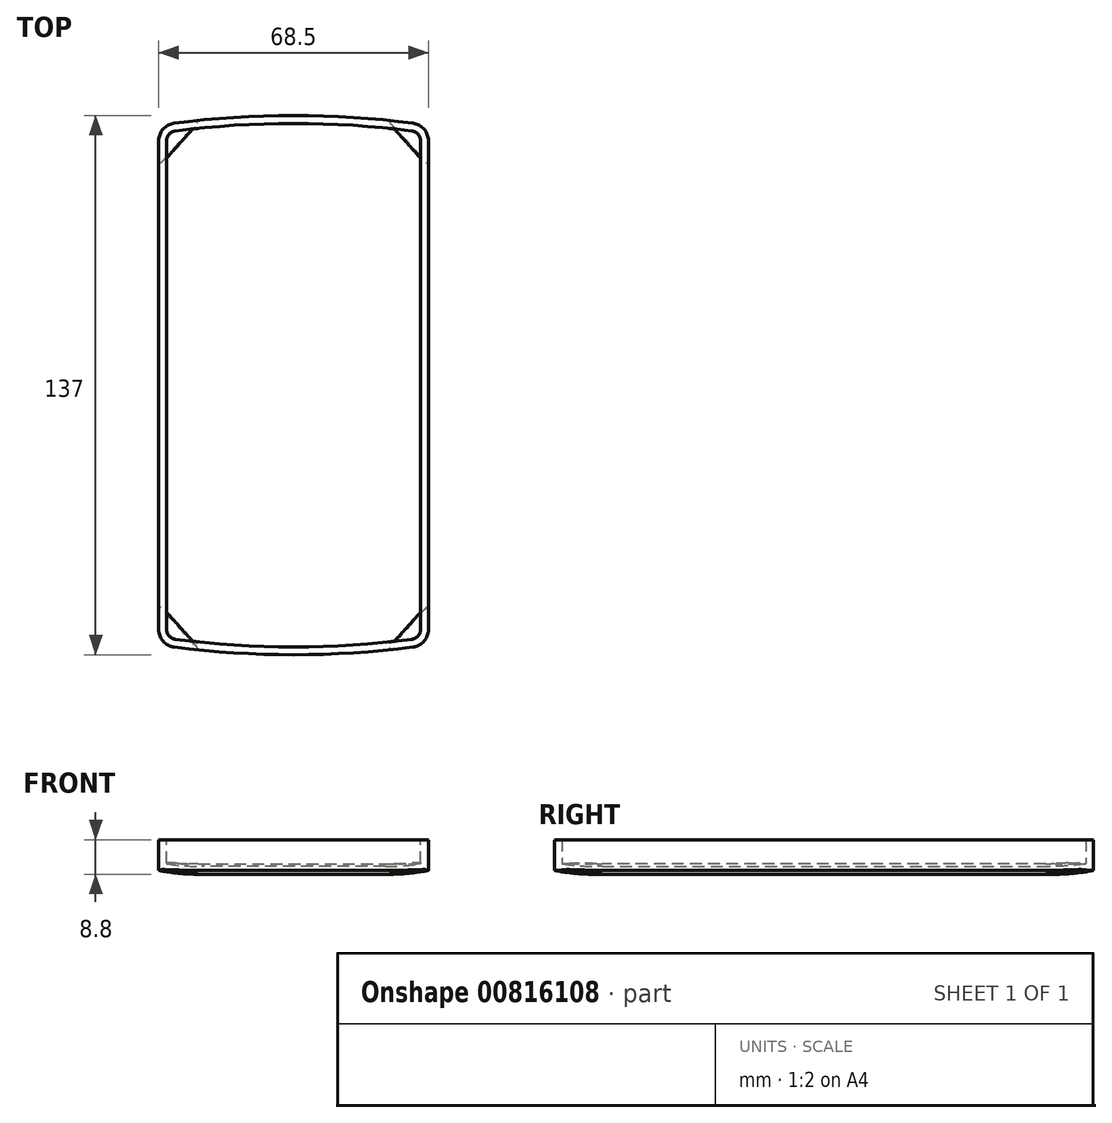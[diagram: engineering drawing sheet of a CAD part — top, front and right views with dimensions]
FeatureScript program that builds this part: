
annotation { "Feature Type Name" : "Feature", "Feature Type Description" : "" }
export const myFeature = defineFeature(function(context is Context, id is Id, definition is map)
    precondition{}
    {
        {
            var Q0;
            Q0=qCreatedBy(makeId("Top.planeOp"),FACE);
            var sketch = newSketch(context, id + "F0", { "sketchPlane" : qUnion([Q0])});
            skLineSegment(sketch, "E0.bottom", {"start": v(34.25, -68.5) * mm, "end": v(-34.25, -68.5) * mm, "construction": true});
            skLineSegment(sketch, "E0.top", {"start": v(34.25, 68.5) * mm, "end": v(-34.25, 68.5) * mm, "construction": true});
            skLineSegment(sketch, "E0.left", {"start": v(34.25, -68.5) * mm, "end": v(34.25, -66) * mm, "construction": true});
            skLineSegment(sketch, "E0.right", {"start": v(-34.25, -68.5) * mm, "end": v(-34.25, -66) * mm, "construction": true});
            skPoint(sketch, "E0.middle", {"position": v(0, 0) * mm});
            skPoint(sketch, "E1", {"position": v(0, -68.5) * mm});
            skPoint(sketch, "E2", {"position": v(0, 68.5) * mm});
            skLineSegment(sketch, "E3", {"start": v(34.25, 66) * mm, "end": v(34.25, 68.5) * mm, "construction": true});
            skLineSegment(sketch, "E4", {"start": v(34.25, -66) * mm, "end": v(34.25, 66) * mm});
            skLineSegment(sketch, "E5", {"start": v(-34.25, -66) * mm, "end": v(-34.25, 66) * mm});
            skLineSegment(sketch, "E6", {"start": v(-34.25, 66) * mm, "end": v(-34.25, 68.5) * mm, "construction": true});
            skArc(sketch, "E7", {"start": v(-34.25, -66) * mm, "mid": v(0, -68.5) * mm, "end": v(34.25, -66) * mm});
            skArc(sketch, "E8", {"start": v(34.25, 66) * mm, "mid": v(0, 68.5) * mm, "end": v(-34.25, 66) * mm});
            skSolve(sketch);
        }
        {
            var Q0;
            Q0=makeQuery(id+"F0.imprint","IMPRINT",FACE,{"disambiguationData":[TD([[makeQuery(id+"F0.imprint","IMPRINT",EDGE,{"derivedFrom":sQuery(id+"F0.wireOp",EDGE,"E0.bottom")}),-1.0]])]});
            var Q1;
            Q1=makeQuery(id+"F0.imprint","IMPRINT",FACE,{"disambiguationData":[TD([[makeQuery(id+"F0.imprint","IMPRINT",EDGE,{"derivedFrom":sQuery(id+"F0.wireOp",EDGE,"E4")}),1.0]])]});
            extrude(context, id + "F1", {"entities" : qUnion([Q0, Q1]), "depth" : 7.8 * mm, "offsetDistance" : 25 * mm});
        }
        {
            var Q0;
            Q0=makeQuery(id+"F1.opExtrude","SWEPT_EDGE",EDGE,{"disambiguationData":[OSD([sQuery(id+"F0.wireOp",EDGE,"E5"),sQuery(id+"F0.wireOp",EDGE,"E7")])]});
            var Q1;
            Q1=makeQuery(id+"F1.opExtrude","SWEPT_EDGE",EDGE,{"disambiguationData":[OSD([sQuery(id+"F0.wireOp",EDGE,"E4"),sQuery(id+"F0.wireOp",EDGE,"E7")])]});
            var Q2;
            Q2=makeQuery(id+"F1.opExtrude","SWEPT_EDGE",EDGE,{"disambiguationData":[OSD([sQuery(id+"F0.wireOp",EDGE,"E5"),sQuery(id+"F0.wireOp",EDGE,"E8")])]});
            var Q3;
            Q3=makeQuery(id+"F1.opExtrude","SWEPT_EDGE",EDGE,{"disambiguationData":[OSD([sQuery(id+"F0.wireOp",EDGE,"E4"),sQuery(id+"F0.wireOp",EDGE,"E8")])]});
            fillet(context, id + "F2", {"entities" : qUnion([Q0, Q1, Q2, Q3]), "radius" : 4.5 * mm, "tangentPropagation" : true, "allowEdgeOverflow" : false});
        }
        {
            var Q0;
            Q0=makeQuery(id+"F1.opExtrude","CAP_FACE",FACE,{"disambiguationData":[OSD([sQuery(id+"F0.wireOp",EDGE,"E4"),sQuery(id+"F0.wireOp",EDGE,"E5"),sQuery(id+"F0.wireOp",EDGE,"E7"),sQuery(id+"F0.wireOp",EDGE,"E8")])],"isStart":true});
            extrude(context, id + "F3", {"entities" : qUnion([Q0]), "operationType" : NewBodyOperationType.ADD, "depth" : 1 * mm, "offsetDistance" : 25 * mm, "hasDraft" : true, "draftAngle" : 80 * degree, "draftPullDirection" : true});
        }
        {
            var Q0;
            Q0=makeQuery(id+"F3.opExtrude","CAP_EDGE",EDGE,{"disambiguationData":[OSD([sQuery(id+"F0.wireOp",EDGE,"E7")])],"isStart":false});
            var Q1;
            Q1=makeQuery(id+"F3.opExtrude","CAP_EDGE",EDGE,{"disambiguationData":[OSD([sQuery(id+"F0.wireOp",EDGE,"E5")])],"isStart":false});
            var Q2;
            Q2=makeQuery(id+"F3.opExtrude","CAP_EDGE",EDGE,{"disambiguationData":[OSD([sQuery(id+"F0.wireOp",EDGE,"E8")])],"isStart":false});
            var Q3;
            Q3=makeQuery(id+"F3.opExtrude","CAP_EDGE",EDGE,{"disambiguationData":[OSD([sQuery(id+"F0.wireOp",EDGE,"E4")])],"isStart":false});
            var Q4;
            {var subQ0=sQuery(id+"F0.wireOp",EDGE,"E8");var subQ1=sQuery(id+"F0.wireOp",EDGE,"E7");var subQ2=sQuery(id+"F0.wireOp",EDGE,"E5");var subQ3=sQuery(id+"F0.wireOp",EDGE,"E4");var subQ4=makeQuery(id+"F1.opExtrude","CAP_FACE",FACE,{"disambiguationData":[OSD([subQ3,subQ2,subQ1,subQ0])],"isStart":true});var subQ5=makeQuery(id+"F1.opExtrude","SWEPT_EDGE",EDGE,{"disambiguationData":[OSD([subQ3,subQ0])]});Q4=makeQuery(id+"F3.*.draft.opDraft","MERGE",EDGE,{"derivedFrom":[makeQuery(id+"F3.opExtrude","SWEPT_EDGE",EDGE,{"disambiguationData":[OSD([subQ3,subQ2,subQ1,subQ0]),TDD([makeQuery(id+"F2.opFillet","BLEND_VERTEX",VERTEX,{"blendedFrom":[subQ5,makeQuery(id+"F1.opExtrude","SWEPT_FACE",FACE,{"disambiguationData":[OSD([subQ3])]}),subQ4],"blendedInto":[makeQuery(id+"F1.opExtrude","SWEPT_FACE",FACE,{"disambiguationData":[OSD([subQ3])]}),subQ4]})])]}),makeQuery(id+"F3.opExtrude","SWEPT_EDGE",EDGE,{"disambiguationData":[OSD([subQ3,subQ2,subQ1,subQ0]),TDD([makeQuery(id+"F2.opFillet","BLEND_VERTEX",VERTEX,{"blendedFrom":[subQ5,subQ4,makeQuery(id+"F1.opExtrude","SWEPT_FACE",FACE,{"disambiguationData":[OSD([subQ0])]})],"blendedInto":[subQ4,makeQuery(id+"F1.opExtrude","SWEPT_FACE",FACE,{"disambiguationData":[OSD([subQ0])]})]})])]})]});}
            var Q5;
            {var subQ0=sQuery(id+"F0.wireOp",EDGE,"E8");var subQ1=sQuery(id+"F0.wireOp",EDGE,"E7");var subQ2=sQuery(id+"F0.wireOp",EDGE,"E5");var subQ3=sQuery(id+"F0.wireOp",EDGE,"E4");Q5=makeQuery(id+"F3.*.draft.opDraft","SPLIT",EDGE,{"derivedFrom":makeQuery(id+"F3.opExtrude","SWEPT_EDGE",EDGE,{"disambiguationData":[OSD([subQ3,subQ2,subQ1,subQ0]),TDD([makeQuery(id+"F2.opFillet","BLEND_VERTEX",VERTEX,{"blendedFrom":[makeQuery(id+"F1.opExtrude","SWEPT_EDGE",EDGE,{"disambiguationData":[OSD([subQ3,subQ0])]}),makeQuery(id+"F1.opExtrude","CAP_FACE",FACE,{"disambiguationData":[OSD([subQ3,subQ2,subQ1,subQ0])],"isStart":true}),makeQuery(id+"F1.opExtrude","SWEPT_FACE",FACE,{"disambiguationData":[OSD([subQ0])]})],"blendedInto":[makeQuery(id+"F1.opExtrude","CAP_FACE",FACE,{"disambiguationData":[OSD([subQ3,subQ2,subQ1,subQ0])],"isStart":true}),makeQuery(id+"F1.opExtrude","SWEPT_FACE",FACE,{"disambiguationData":[OSD([subQ0])]})]})])]})});}
            var Q6;
            {var subQ0=sQuery(id+"F0.wireOp",EDGE,"E8");var subQ1=sQuery(id+"F0.wireOp",EDGE,"E7");var subQ2=sQuery(id+"F0.wireOp",EDGE,"E5");var subQ3=sQuery(id+"F0.wireOp",EDGE,"E4");Q6=makeQuery(id+"F3.*.draft.opDraft","SPLIT",EDGE,{"derivedFrom":makeQuery(id+"F3.opExtrude","SWEPT_EDGE",EDGE,{"disambiguationData":[OSD([subQ3,subQ2,subQ1,subQ0]),TDD([makeQuery(id+"F2.opFillet","BLEND_VERTEX",VERTEX,{"blendedFrom":[makeQuery(id+"F1.opExtrude","SWEPT_EDGE",EDGE,{"disambiguationData":[OSD([subQ3,subQ0])]}),makeQuery(id+"F1.opExtrude","SWEPT_FACE",FACE,{"disambiguationData":[OSD([subQ3])]}),makeQuery(id+"F1.opExtrude","CAP_FACE",FACE,{"disambiguationData":[OSD([subQ3,subQ2,subQ1,subQ0])],"isStart":true})],"blendedInto":[makeQuery(id+"F1.opExtrude","SWEPT_FACE",FACE,{"disambiguationData":[OSD([subQ3])]}),makeQuery(id+"F1.opExtrude","CAP_FACE",FACE,{"disambiguationData":[OSD([subQ3,subQ2,subQ1,subQ0])],"isStart":true})]})])]})});}
            var Q7;
            {var subQ0=sQuery(id+"F0.wireOp",EDGE,"E8");var subQ1=sQuery(id+"F0.wireOp",EDGE,"E7");var subQ2=sQuery(id+"F0.wireOp",EDGE,"E5");var subQ3=sQuery(id+"F0.wireOp",EDGE,"E4");var subQ4=makeQuery(id+"F1.opExtrude","CAP_FACE",FACE,{"disambiguationData":[OSD([subQ3,subQ2,subQ1,subQ0])],"isStart":true});var subQ5=makeQuery(id+"F1.opExtrude","SWEPT_EDGE",EDGE,{"disambiguationData":[OSD([subQ2,subQ0])]});Q7=makeQuery(id+"F3.*.draft.opDraft","MERGE",EDGE,{"derivedFrom":[makeQuery(id+"F3.opExtrude","SWEPT_EDGE",EDGE,{"disambiguationData":[OSD([subQ3,subQ2,subQ1,subQ0]),TDD([makeQuery(id+"F2.opFillet","BLEND_VERTEX",VERTEX,{"blendedFrom":[subQ5,subQ4,makeQuery(id+"F1.opExtrude","SWEPT_FACE",FACE,{"disambiguationData":[OSD([subQ2])]})],"blendedInto":[subQ4,makeQuery(id+"F1.opExtrude","SWEPT_FACE",FACE,{"disambiguationData":[OSD([subQ2])]})]})])]}),makeQuery(id+"F3.opExtrude","SWEPT_EDGE",EDGE,{"disambiguationData":[OSD([subQ3,subQ2,subQ1,subQ0]),TDD([makeQuery(id+"F2.opFillet","BLEND_VERTEX",VERTEX,{"blendedFrom":[subQ5,subQ4,makeQuery(id+"F1.opExtrude","SWEPT_FACE",FACE,{"disambiguationData":[OSD([subQ0])]})],"blendedInto":[subQ4,makeQuery(id+"F1.opExtrude","SWEPT_FACE",FACE,{"disambiguationData":[OSD([subQ0])]})]})])]})]});}
            var Q8;
            {var subQ0=sQuery(id+"F0.wireOp",EDGE,"E8");var subQ1=sQuery(id+"F0.wireOp",EDGE,"E7");var subQ2=sQuery(id+"F0.wireOp",EDGE,"E5");var subQ3=sQuery(id+"F0.wireOp",EDGE,"E4");Q8=makeQuery(id+"F3.*.draft.opDraft","SPLIT",EDGE,{"derivedFrom":makeQuery(id+"F3.opExtrude","SWEPT_EDGE",EDGE,{"disambiguationData":[OSD([subQ3,subQ2,subQ1,subQ0]),TDD([makeQuery(id+"F2.opFillet","BLEND_VERTEX",VERTEX,{"blendedFrom":[makeQuery(id+"F1.opExtrude","SWEPT_EDGE",EDGE,{"disambiguationData":[OSD([subQ2,subQ0])]}),makeQuery(id+"F1.opExtrude","CAP_FACE",FACE,{"disambiguationData":[OSD([subQ3,subQ2,subQ1,subQ0])],"isStart":true}),makeQuery(id+"F1.opExtrude","SWEPT_FACE",FACE,{"disambiguationData":[OSD([subQ0])]})],"blendedInto":[makeQuery(id+"F1.opExtrude","CAP_FACE",FACE,{"disambiguationData":[OSD([subQ3,subQ2,subQ1,subQ0])],"isStart":true}),makeQuery(id+"F1.opExtrude","SWEPT_FACE",FACE,{"disambiguationData":[OSD([subQ0])]})]})])]})});}
            var Q9;
            {var subQ0=sQuery(id+"F0.wireOp",EDGE,"E5");var subQ1=sQuery(id+"F0.wireOp",EDGE,"E8");var subQ2=sQuery(id+"F0.wireOp",EDGE,"E7");var subQ3=sQuery(id+"F0.wireOp",EDGE,"E4");Q9=makeQuery(id+"F3.*.draft.opDraft","SPLIT",EDGE,{"derivedFrom":makeQuery(id+"F3.opExtrude","SWEPT_EDGE",EDGE,{"disambiguationData":[OSD([subQ3,subQ0,subQ2,subQ1]),TDD([makeQuery(id+"F2.opFillet","BLEND_VERTEX",VERTEX,{"blendedFrom":[makeQuery(id+"F1.opExtrude","SWEPT_EDGE",EDGE,{"disambiguationData":[OSD([subQ0,subQ1])]}),makeQuery(id+"F1.opExtrude","CAP_FACE",FACE,{"disambiguationData":[OSD([subQ3,subQ0,subQ2,subQ1])],"isStart":true}),makeQuery(id+"F1.opExtrude","SWEPT_FACE",FACE,{"disambiguationData":[OSD([subQ0])]})],"blendedInto":[makeQuery(id+"F1.opExtrude","CAP_FACE",FACE,{"disambiguationData":[OSD([subQ3,subQ0,subQ2,subQ1])],"isStart":true}),makeQuery(id+"F1.opExtrude","SWEPT_FACE",FACE,{"disambiguationData":[OSD([subQ0])]})]})])]})});}
            var Q10;
            {var subQ0=sQuery(id+"F0.wireOp",EDGE,"E5");var subQ1=sQuery(id+"F0.wireOp",EDGE,"E8");var subQ2=sQuery(id+"F0.wireOp",EDGE,"E7");var subQ3=sQuery(id+"F0.wireOp",EDGE,"E4");Q10=makeQuery(id+"F3.*.draft.opDraft","SPLIT",EDGE,{"derivedFrom":makeQuery(id+"F3.opExtrude","SWEPT_EDGE",EDGE,{"disambiguationData":[OSD([subQ3,subQ0,subQ2,subQ1]),TDD([makeQuery(id+"F2.opFillet","BLEND_VERTEX",VERTEX,{"blendedFrom":[makeQuery(id+"F1.opExtrude","SWEPT_EDGE",EDGE,{"disambiguationData":[OSD([subQ0,subQ2])]}),makeQuery(id+"F1.opExtrude","CAP_FACE",FACE,{"disambiguationData":[OSD([subQ3,subQ0,subQ2,subQ1])],"isStart":true}),makeQuery(id+"F1.opExtrude","SWEPT_FACE",FACE,{"disambiguationData":[OSD([subQ0])]})],"blendedInto":[makeQuery(id+"F1.opExtrude","CAP_FACE",FACE,{"disambiguationData":[OSD([subQ3,subQ0,subQ2,subQ1])],"isStart":true}),makeQuery(id+"F1.opExtrude","SWEPT_FACE",FACE,{"disambiguationData":[OSD([subQ0])]})]})])]})});}
            var Q11;
            {var subQ0=sQuery(id+"F0.wireOp",EDGE,"E7");var subQ1=sQuery(id+"F0.wireOp",EDGE,"E8");var subQ2=sQuery(id+"F0.wireOp",EDGE,"E5");var subQ3=sQuery(id+"F0.wireOp",EDGE,"E4");Q11=makeQuery(id+"F3.*.draft.opDraft","SPLIT",EDGE,{"derivedFrom":makeQuery(id+"F3.opExtrude","SWEPT_EDGE",EDGE,{"disambiguationData":[OSD([subQ3,subQ2,subQ0,subQ1]),TDD([makeQuery(id+"F2.opFillet","BLEND_VERTEX",VERTEX,{"blendedFrom":[makeQuery(id+"F1.opExtrude","SWEPT_EDGE",EDGE,{"disambiguationData":[OSD([subQ2,subQ0])]}),makeQuery(id+"F1.opExtrude","CAP_FACE",FACE,{"disambiguationData":[OSD([subQ3,subQ2,subQ0,subQ1])],"isStart":true}),makeQuery(id+"F1.opExtrude","SWEPT_FACE",FACE,{"disambiguationData":[OSD([subQ0])]})],"blendedInto":[makeQuery(id+"F1.opExtrude","CAP_FACE",FACE,{"disambiguationData":[OSD([subQ3,subQ2,subQ0,subQ1])],"isStart":true}),makeQuery(id+"F1.opExtrude","SWEPT_FACE",FACE,{"disambiguationData":[OSD([subQ0])]})]})])]})});}
            var Q12;
            {var subQ0=sQuery(id+"F0.wireOp",EDGE,"E7");var subQ1=sQuery(id+"F0.wireOp",EDGE,"E8");var subQ2=sQuery(id+"F0.wireOp",EDGE,"E5");var subQ3=sQuery(id+"F0.wireOp",EDGE,"E4");var subQ4=makeQuery(id+"F1.opExtrude","CAP_FACE",FACE,{"disambiguationData":[OSD([subQ3,subQ2,subQ0,subQ1])],"isStart":true});var subQ5=makeQuery(id+"F1.opExtrude","SWEPT_EDGE",EDGE,{"disambiguationData":[OSD([subQ2,subQ0])]});Q12=makeQuery(id+"F3.*.draft.opDraft","MERGE",EDGE,{"derivedFrom":[makeQuery(id+"F3.opExtrude","SWEPT_EDGE",EDGE,{"disambiguationData":[OSD([subQ3,subQ2,subQ0,subQ1]),TDD([makeQuery(id+"F2.opFillet","BLEND_VERTEX",VERTEX,{"blendedFrom":[subQ5,subQ4,makeQuery(id+"F1.opExtrude","SWEPT_FACE",FACE,{"disambiguationData":[OSD([subQ2])]})],"blendedInto":[subQ4,makeQuery(id+"F1.opExtrude","SWEPT_FACE",FACE,{"disambiguationData":[OSD([subQ2])]})]})])]}),makeQuery(id+"F3.opExtrude","SWEPT_EDGE",EDGE,{"disambiguationData":[OSD([subQ3,subQ2,subQ0,subQ1]),TDD([makeQuery(id+"F2.opFillet","BLEND_VERTEX",VERTEX,{"blendedFrom":[subQ5,subQ4,makeQuery(id+"F1.opExtrude","SWEPT_FACE",FACE,{"disambiguationData":[OSD([subQ0])]})],"blendedInto":[subQ4,makeQuery(id+"F1.opExtrude","SWEPT_FACE",FACE,{"disambiguationData":[OSD([subQ0])]})]})])]})]});}
            var Q13;
            {var subQ0=sQuery(id+"F0.wireOp",EDGE,"E7");var subQ1=sQuery(id+"F0.wireOp",EDGE,"E8");var subQ2=sQuery(id+"F0.wireOp",EDGE,"E5");var subQ3=sQuery(id+"F0.wireOp",EDGE,"E4");var subQ4=makeQuery(id+"F1.opExtrude","CAP_FACE",FACE,{"disambiguationData":[OSD([subQ3,subQ2,subQ0,subQ1])],"isStart":true});var subQ5=makeQuery(id+"F1.opExtrude","SWEPT_EDGE",EDGE,{"disambiguationData":[OSD([subQ3,subQ0])]});Q13=makeQuery(id+"F3.*.draft.opDraft","MERGE",EDGE,{"derivedFrom":[makeQuery(id+"F3.opExtrude","SWEPT_EDGE",EDGE,{"disambiguationData":[OSD([subQ3,subQ2,subQ0,subQ1]),TDD([makeQuery(id+"F2.opFillet","BLEND_VERTEX",VERTEX,{"blendedFrom":[subQ5,makeQuery(id+"F1.opExtrude","SWEPT_FACE",FACE,{"disambiguationData":[OSD([subQ3])]}),subQ4],"blendedInto":[makeQuery(id+"F1.opExtrude","SWEPT_FACE",FACE,{"disambiguationData":[OSD([subQ3])]}),subQ4]})])]}),makeQuery(id+"F3.opExtrude","SWEPT_EDGE",EDGE,{"disambiguationData":[OSD([subQ3,subQ2,subQ0,subQ1]),TDD([makeQuery(id+"F2.opFillet","BLEND_VERTEX",VERTEX,{"blendedFrom":[subQ5,subQ4,makeQuery(id+"F1.opExtrude","SWEPT_FACE",FACE,{"disambiguationData":[OSD([subQ0])]})],"blendedInto":[subQ4,makeQuery(id+"F1.opExtrude","SWEPT_FACE",FACE,{"disambiguationData":[OSD([subQ0])]})]})])]})]});}
            var Q14;
            {var subQ0=sQuery(id+"F0.wireOp",EDGE,"E7");var subQ1=sQuery(id+"F0.wireOp",EDGE,"E8");var subQ2=sQuery(id+"F0.wireOp",EDGE,"E5");var subQ3=sQuery(id+"F0.wireOp",EDGE,"E4");Q14=makeQuery(id+"F3.*.draft.opDraft","SPLIT",EDGE,{"derivedFrom":makeQuery(id+"F3.opExtrude","SWEPT_EDGE",EDGE,{"disambiguationData":[OSD([subQ3,subQ2,subQ0,subQ1]),TDD([makeQuery(id+"F2.opFillet","BLEND_VERTEX",VERTEX,{"blendedFrom":[makeQuery(id+"F1.opExtrude","SWEPT_EDGE",EDGE,{"disambiguationData":[OSD([subQ3,subQ0])]}),makeQuery(id+"F1.opExtrude","CAP_FACE",FACE,{"disambiguationData":[OSD([subQ3,subQ2,subQ0,subQ1])],"isStart":true}),makeQuery(id+"F1.opExtrude","SWEPT_FACE",FACE,{"disambiguationData":[OSD([subQ0])]})],"blendedInto":[makeQuery(id+"F1.opExtrude","CAP_FACE",FACE,{"disambiguationData":[OSD([subQ3,subQ2,subQ0,subQ1])],"isStart":true}),makeQuery(id+"F1.opExtrude","SWEPT_FACE",FACE,{"disambiguationData":[OSD([subQ0])]})]})])]})});}
            var Q15;
            {var subQ0=sQuery(id+"F0.wireOp",EDGE,"E8");var subQ1=sQuery(id+"F0.wireOp",EDGE,"E7");var subQ2=sQuery(id+"F0.wireOp",EDGE,"E5");var subQ3=sQuery(id+"F0.wireOp",EDGE,"E4");Q15=makeQuery(id+"F3.*.draft.opDraft","SPLIT",EDGE,{"derivedFrom":makeQuery(id+"F3.opExtrude","SWEPT_EDGE",EDGE,{"disambiguationData":[OSD([subQ3,subQ2,subQ1,subQ0]),TDD([makeQuery(id+"F2.opFillet","BLEND_VERTEX",VERTEX,{"blendedFrom":[makeQuery(id+"F1.opExtrude","SWEPT_EDGE",EDGE,{"disambiguationData":[OSD([subQ3,subQ1])]}),makeQuery(id+"F1.opExtrude","SWEPT_FACE",FACE,{"disambiguationData":[OSD([subQ3])]}),makeQuery(id+"F1.opExtrude","CAP_FACE",FACE,{"disambiguationData":[OSD([subQ3,subQ2,subQ1,subQ0])],"isStart":true})],"blendedInto":[makeQuery(id+"F1.opExtrude","SWEPT_FACE",FACE,{"disambiguationData":[OSD([subQ3])]}),makeQuery(id+"F1.opExtrude","CAP_FACE",FACE,{"disambiguationData":[OSD([subQ3,subQ2,subQ1,subQ0])],"isStart":true})]})])]})});}
            fillet(context, id + "F4", {"entities" : qUnion([Q0, Q1, Q2, Q3, Q4, Q5, Q6, Q7, Q8, Q9, Q10, Q11, Q12, Q13, Q14, Q15]), "radius" : 60 * mm, "tangentPropagation" : true, "allowEdgeOverflow" : false});
        }
        {
            var Q0;
            Q0=makeQuery(id+"F1.opExtrude","CAP_FACE",FACE,{"disambiguationData":[OSD([sQuery(id+"F0.wireOp",EDGE,"E4"),sQuery(id+"F0.wireOp",EDGE,"E5"),sQuery(id+"F0.wireOp",EDGE,"E7"),sQuery(id+"F0.wireOp",EDGE,"E8")])],"isStart":false});
            shell(context, id + "F5", {"entities" : qUnion([Q0]), "thickness" : 2 * mm});
        }
    });
